# Revit family: LSER14
name_source: partatom
category: Lighting Fixtures
revit_build: Autodesk Revit MEP 2012 (Build: 20110309_2315(x64)
units: mm (PartAtom-declared; Revit-internal decimal feet)

## types (24) — shared parameters
Apparent Load = 0 VA
Color Filter = 16777215
Default Elevation = 4' - 0"
Dimming Lamp Color Temperature Shift = <None>
IES FILE LINK = http://www.columbialighting.com
LEGNTH = 4' - 6"
Lamp = LED
Manufacturer = COLUMBIA
Model = LSER14
Number of Poles = 1
Power Factor = 1
Product Documentation Link = http://www.columbialighting.com
Product Page URL = http://www.columbialighting.com
Tilt Angle = 90.00°
Voltage = 0 V
WIDTH = 2' - 0"

## per-type parameters (varying)
| type | Photometric Web File |
| LSER14-40VLG-R-ESD | itl78348.ies |
| LSER14-40VLG-C-ESD | itl78345.ies |
| LSER14-40MLG-R-ESD | itl78336.ies |
| LSER14-40MLG-C-ESD | itl78333.ies |
| LSER14-40LWG-R-ESD | itl78330.ies |
| LSER14-40LWG-C-ESD | itl78327.ies |
| LSER14-40HLG-R-ESD | itl78342.ies |
| LSER14-40HLG-C-ESD | itl78339.ies |
| LSER14-35VLG-R-ESD | itl78347.ies |
| LSER14-35VLG-C-ESD | itl78344.ies |
| LSER14-35MLG-R-ESD | itl78335.ies |
| LSER14-35MLG-C-ESD | itl78332.ies |
| LSER14-35LWG-R-ESD | itl78329.ies |
| LSER14-35LWG-C-ESD | itl78326.ies |
| LSER14-35HLG-R-ESD | itl78341.ies |
| LSER14-35HLG-C-ESD | itl78338.ies |
| LSER14-30VLG-R-ESD | itl78346.ies |
| LSER14-30VLG-C-ESD | itl78343.ies |
| LSER14-30MLG-R-ESD | itl78334.ies |
| LSER14-30MLG-C-ESD | itl78331.ies |
| LSER14-30LWG-R-ESD | itl78328.ies |
| LSER14-30LWG-C-ESD | itl78325.ies |
| LSER14-30HLG-R-ESD | itl78340.ies |
| LSER14-30HLG-C-ESD | itl78337.ies |

## geometry (parser evidence)
native form markers: Sweep x2
no freeform markers — native parametric forms only
